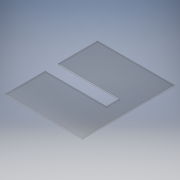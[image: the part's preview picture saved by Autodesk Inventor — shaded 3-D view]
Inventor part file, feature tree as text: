
AUTODESK INVENTOR PART (.ipt)
format: ipt  version: 2019 (Build 230136000, 136)  size: 116,224 bytes
history: native  units: in
note: dims shown in document units (in); Inventor stores cm internally (conversion verified against a paired STEP export)
features: extrude x1, sketch x1
ambient origin geometry x8: Origin, YZ Plane, XZ Plane, XY Plane, X Axis, Y Axis, Z Axis, Center Point
bodies: Solid1 (feature_tree)
feature tree (2):
  extrude  "Extrusion1"  Depth=5.0in
  sketch  "Sketch1"  dims[d0=6.0in d1=5.0in d2=0.85in d3=2.575in d4=4.0in d5=0.073in d6=0.0in]
